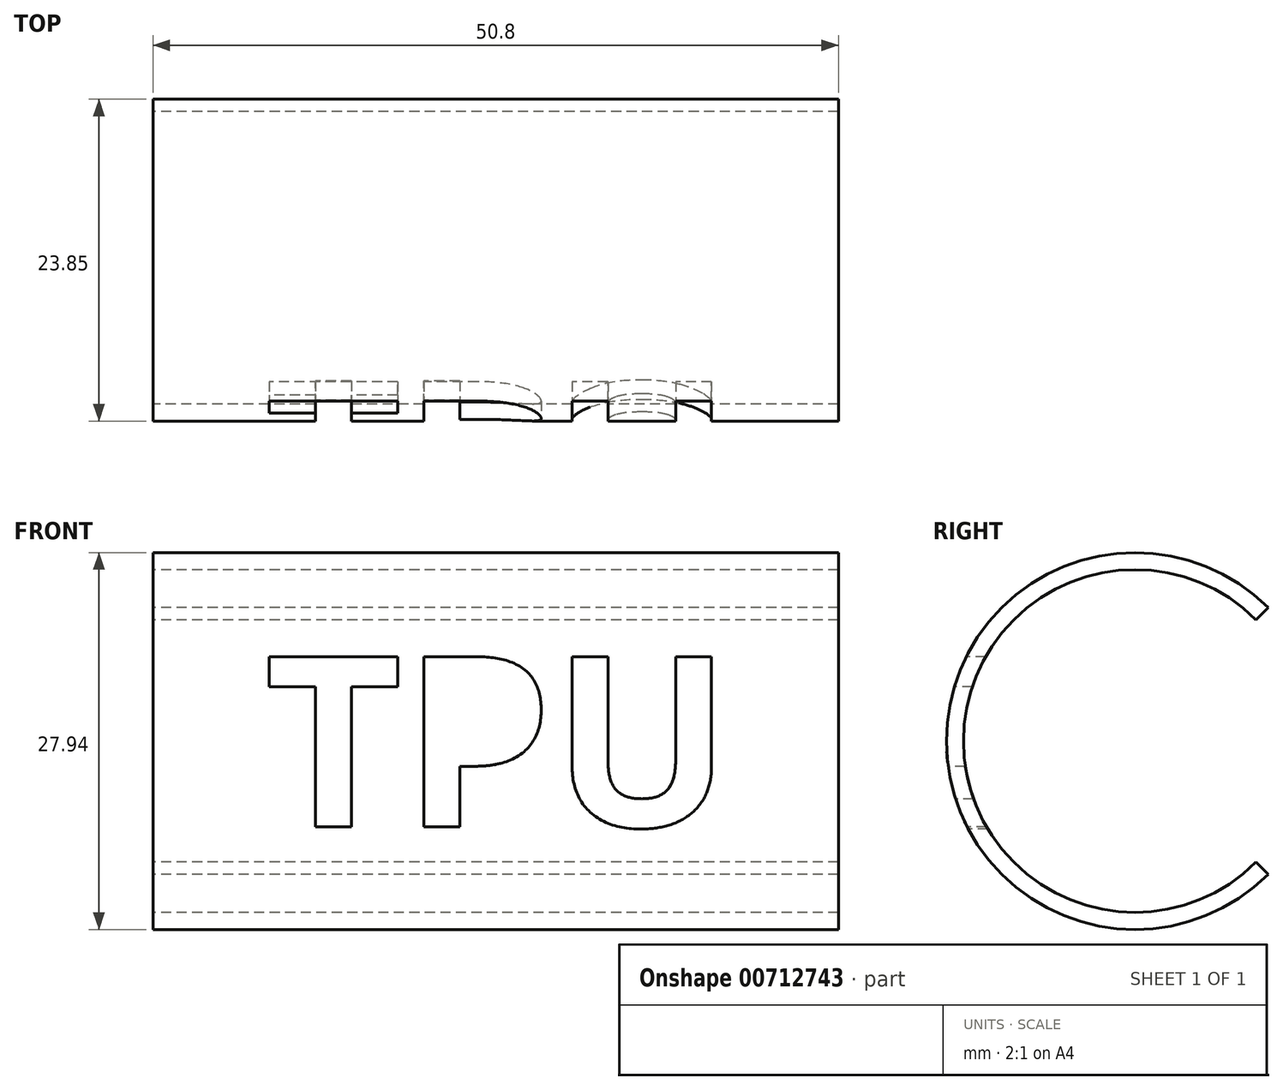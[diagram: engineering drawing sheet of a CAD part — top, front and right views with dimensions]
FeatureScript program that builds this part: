
annotation { "Feature Type Name" : "Feature", "Feature Type Description" : "" }
export const myFeature = defineFeature(function(context is Context, id is Id, definition is map)
    precondition{}
    {
        {
            var Q0;
            Q0=qCreatedBy(makeId("Right.planeOp"),FACE);
            var sketch = newSketch(context, id + "F0", { "sketchPlane" : qUnion([Q0])});
            skCircle(sketch, "E0", {"center": v(0, 0) * mm, "radius": 12.7 * mm});
            skCircle(sketch, "E1", {"center": v(0, 0) * mm, "radius": 13.97 * mm});
            skLineSegment(sketch, "E2", {"start": v(0, 0) * mm, "end": v(13.97, 0) * mm});
            skLineSegment(sketch, "E3", {"start": v(0, 0) * mm, "end": v(9.88, 9.88) * mm});
            skLineSegment(sketch, "E4.MirrorCS", {"start": v(0, 0) * mm, "end": v(9.88, -9.88) * mm});
            skSolve(sketch);
        }
        {
            var Q0;
            {var subQ0=sQuery(id+"F0.wireOp",EDGE,"E3");var subQ1=sQuery(id+"F0.wireOp",EDGE,"E0");var subQ2=makeQuery(id+"F0.imprint","INTERSECT",VERTEX,{"derivedFrom":[subQ1,subQ0]});Q0=makeQuery(id+"F0.imprint","IMPRINT",FACE,{"disambiguationData":[TD([[makeQuery(id+"F0.imprint","IMPRINT",EDGE,{"disambiguationData":[TD([[subQ2,-1.0]])],"derivedFrom":subQ1}),-1.0]])]});}
            extrude(context, id + "F1", {"entities" : qUnion([Q0]), "depth" : 50.8 * mm, "offsetDistance" : 25.4 * mm});
        }
        {
            var Q0;
            Q0=qCreatedBy(makeId("Front.planeOp"),FACE);
            cPlane(context, id + "F2", {"entities" : qUnion([Q0]), "cplaneType" : CPlaneType.OFFSET, "offset" : 25.4 * mm, "width" : 152.4 * mm, "height" : 152.4 * mm});
        }
        {
            var Q0;
            Q0=qCreatedBy(id+"F2.planeOp",FACE);
            var sketch = newSketch(context, id + "F3", { "sketchPlane" : qUnion([Q0])});
            skLineSegment(sketch, "E5.bottom", {"start": v(0, 13.97) * mm, "end": v(50.8, 13.97) * mm});
            skLineSegment(sketch, "E5.top", {"start": v(0, -13.97) * mm, "end": v(50.8, -13.97) * mm});
            skLineSegment(sketch, "E5.left", {"start": v(0, 13.97) * mm, "end": v(0, -13.97) * mm});
            skLineSegment(sketch, "E5.right", {"start": v(50.8, 13.97) * mm, "end": v(50.8, -13.97) * mm});
            skPoint(sketch, "E6", {"position": v(25.4, 13.97) * mm});
            skText(sketch, "E7", { "text": "TPU", "fontName": "OpenSans-Bold.ttf"});
            const initialGuessF3  = {"E7": [0.00827, -0.00635, 1, 0, 0.0127]};
            skSetInitialGuess(sketch, initialGuessF3);
            skSolve(sketch);
        }
        {
            var Q0;
            Q0=makeQuery(id+"F3.imprint","IMPRINT",FACE,{"disambiguationData":[TD([[makeQuery(id+"F3.imprint","IMPRINT",EDGE,{"derivedFrom":sQuery(id+"F3.wireOp",EDGE,"E7.sketch_text.stroke-0")}),-1.0]])]});
            var Q1;
            Q1=makeQuery(id+"F3.imprint","IMPRINT",FACE,{"disambiguationData":[TD([[makeQuery(id+"F3.imprint","IMPRINT",EDGE,{"derivedFrom":sQuery(id+"F3.wireOp",EDGE,"E7.sketch_text.stroke-16")}),-1.0]])]});
            var Q2;
            Q2=makeQuery(id+"F3.imprint","IMPRINT",FACE,{"disambiguationData":[TD([[makeQuery(id+"F3.imprint","IMPRINT",EDGE,{"derivedFrom":sQuery(id+"F3.wireOp",EDGE,"E7.sketch_text.stroke-28")}),-1.0]])]});
            var Q3;
            Q3=makeQuery(id+"F3.imprint","IMPRINT",FACE,{"disambiguationData":[TD([[makeQuery(id+"F3.imprint","IMPRINT",EDGE,{"derivedFrom":sQuery(id+"F3.wireOp",EDGE,"E7.sketch_text.stroke-36")}),-1.0]])]});
            var Q4;
            Q4=makeQuery(id+"F3.imprint","IMPRINT",FACE,{"disambiguationData":[TD([[makeQuery(id+"F3.imprint","IMPRINT",EDGE,{"derivedFrom":sQuery(id+"F3.wireOp",EDGE,"E7.sketch_text.stroke-8")}),1.0]])]});
            extrude(context, id + "F4", {"entities" : qUnion([Q0, Q1, Q2, Q3, Q4]), "operationType" : NewBodyOperationType.REMOVE, "endBound" : BoundingType.THROUGH_ALL, "oppositeDirection" : true, "depth" : 25.4 * mm, "offsetDistance" : 25.4 * mm});
        }
    });
